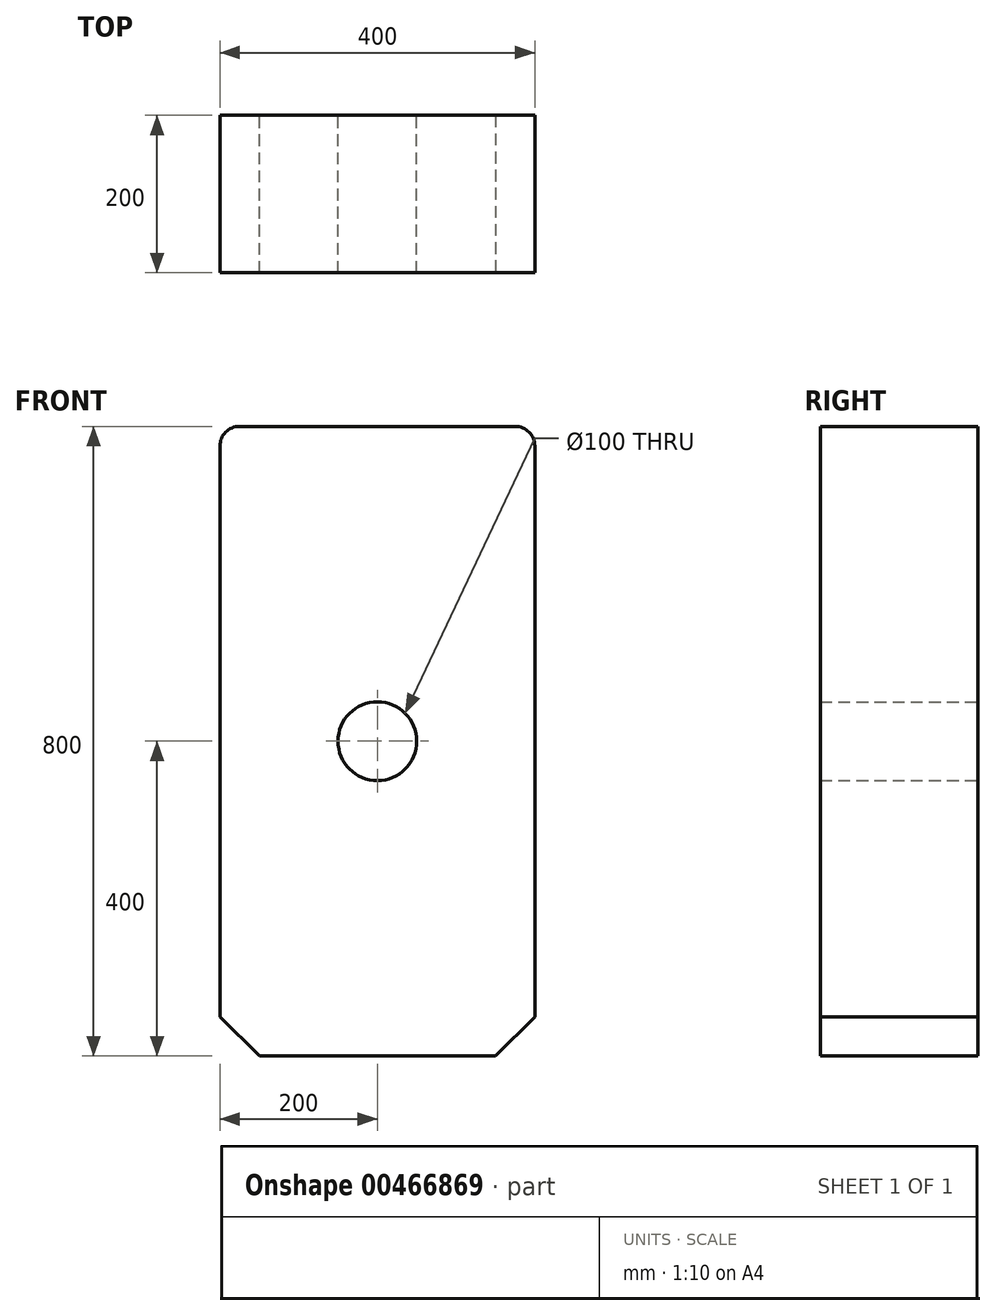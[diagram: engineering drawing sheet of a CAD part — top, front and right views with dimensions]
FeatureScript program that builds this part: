
annotation { "Feature Type Name" : "Feature", "Feature Type Description" : "" }
export const myFeature = defineFeature(function(context is Context, id is Id, definition is map)
    precondition{}
    {
        {
            var Q0;
            Q0=qCreatedBy(makeId("Front.planeOp"),FACE);
            var sketch = newSketch(context, id + "F0", { "sketchPlane" : qUnion([Q0])});
            skLineSegment(sketch, "E0.bottom", {"start": v(200, 400) * mm, "end": v(-200, 400) * mm});
            skLineSegment(sketch, "E0.top", {"start": v(200, -400) * mm, "end": v(-200, -400) * mm});
            skLineSegment(sketch, "E0.left", {"start": v(200, 400) * mm, "end": v(200, -400) * mm});
            skLineSegment(sketch, "E0.right", {"start": v(-200, 400) * mm, "end": v(-200, -400) * mm});
            skPoint(sketch, "E0.middle", {"position": v(0, 0) * mm});
            skSolve(sketch);
        }
        {
            var Q0;
            Q0 = qSketchRegion(id + "F0", true);
            extrude(context, id + "F1", {"entities" : qUnion([Q0]), "depth" : 200 * mm});
        }
        {
            var Q0;
            Q0=qCreatedBy(makeId("Front.planeOp"),FACE);
            var sketch = newSketch(context, id + "F2", { "sketchPlane" : qUnion([Q0])});
            skCircle(sketch, "E1", {"center": v(0, 0) * mm, "radius": 50 * mm});
            skSolve(sketch);
        }
        {
            var Q0;
            Q0 = qSketchRegion(id + "F2", true);
            extrude(context, id + "F3", {"entities" : qUnion([Q0]), "operationType" : NewBodyOperationType.REMOVE, "depth" : 250 * mm});
        }
        {
            var Q0;
            Q0=makeQuery(id+"F1.opExtrude","SWEPT_EDGE",EDGE,{"disambiguationData":[OSD([sQuery(id+"F0.wireOp",EDGE,"E0.top"),sQuery(id+"F0.wireOp",EDGE,"E0.right")])]});
            chamfer(context, id + "F4", {"entities" : qUnion([Q0]), "width" : 50 * mm, "tangentPropagation" : true});
        }
        {
            var Q0;
            Q0=makeQuery(id+"F1.opExtrude","SWEPT_EDGE",EDGE,{"disambiguationData":[OSD([sQuery(id+"F0.wireOp",EDGE,"E0.top"),sQuery(id+"F0.wireOp",EDGE,"E0.left")])]});
            chamfer(context, id + "F5", {"entities" : qUnion([Q0]), "width" : 50 * mm, "tangentPropagation" : true});
        }
        {
            var Q0;
            Q0=makeQuery(id+"F1.opExtrude","SWEPT_EDGE",EDGE,{"disambiguationData":[OSD([sQuery(id+"F0.wireOp",EDGE,"E0.bottom"),sQuery(id+"F0.wireOp",EDGE,"E0.left")])]});
            fillet(context, id + "F6", {"entities" : qUnion([Q0]), "radius" : 25 * mm, "tangentPropagation" : true, "allowEdgeOverflow" : false});
        }
        {
            var Q0;
            Q0=makeQuery(id+"F1.opExtrude","SWEPT_EDGE",EDGE,{"disambiguationData":[OSD([sQuery(id+"F0.wireOp",EDGE,"E0.bottom"),sQuery(id+"F0.wireOp",EDGE,"E0.right")])]});
            fillet(context, id + "F7", {"entities" : qUnion([Q0]), "radius" : 25 * mm, "tangentPropagation" : true, "allowEdgeOverflow" : false});
        }
    });
